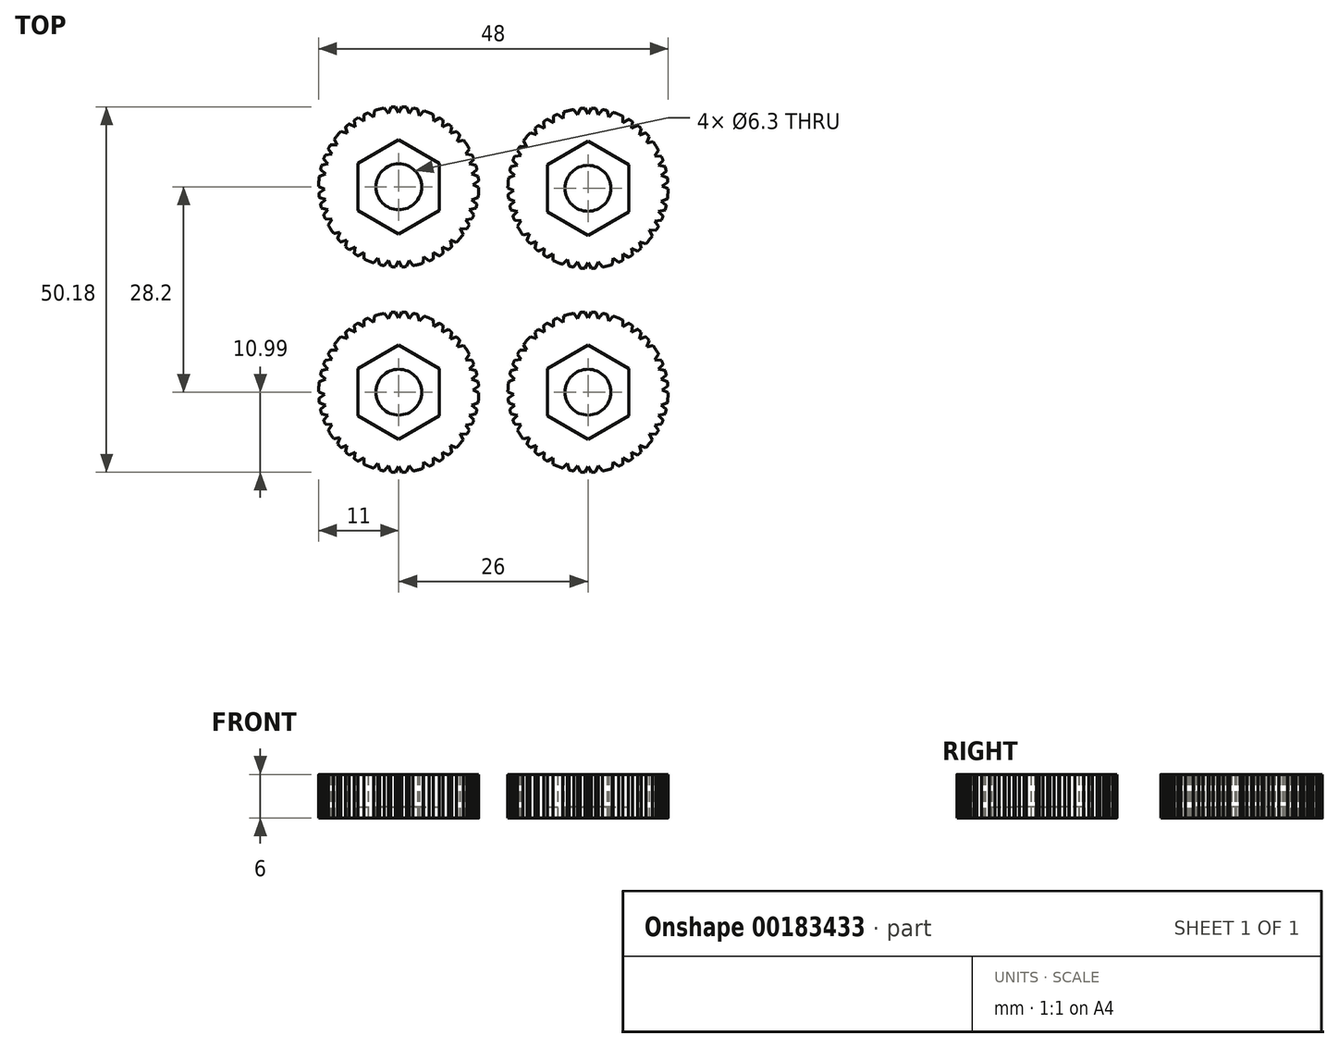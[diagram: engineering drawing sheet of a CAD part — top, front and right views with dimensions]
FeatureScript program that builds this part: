
annotation { "Feature Type Name" : "Feature", "Feature Type Description" : "" }
export const myFeature = defineFeature(function(context is Context, id is Id, definition is map)
    precondition{}
    {
        {
            var Q0;
            Q0=qCreatedBy(makeId("Top.planeOp"),FACE);
            var sketch = newSketch(context, id + "F0", { "sketchPlane" : qUnion([Q0])});
            skCircle(sketch, "E0", {"center": v(0, 0) * mm, "radius": 11 * mm});
            skCircle(sketch, "E1.cCircle", {"center": v(0, 11) * mm, "radius": 0.4 * mm, "construction": true});
            skLineSegment(sketch, "E1.0", {"start": v(-0.7, 11.4) * mm, "end": v(0.7, 11.4) * mm});
            skLineSegment(sketch, "E1.1", {"start": v(0.7, 11.4) * mm, "end": v(0, 10.2) * mm});
            skLineSegment(sketch, "E1.2", {"start": v(0, 10.2) * mm, "end": v(-0.7, 11.4) * mm});
            skPoint(sketch, "E1.0.midPoint", {"position": v(0, 11.4) * mm});
            skLineSegment(sketch, "E2.1.0", {"start": v(-6, 8.25) * mm, "end": v(-7.26, 8.82) * mm});
            skCircle(sketch, "E2.1.1", {"center": v(-6.47, 8.9) * mm, "radius": 0.4 * mm, "construction": true});
            skPoint(sketch, "E2.1.2", {"position": v(-6.7, 9.22) * mm});
            skLineSegment(sketch, "E2.1.3", {"start": v(-7.26, 8.82) * mm, "end": v(-6.14, 9.63) * mm});
            skLineSegment(sketch, "E2.1.4", {"start": v(-6.14, 9.63) * mm, "end": v(-6, 8.25) * mm});
            skLineSegment(sketch, "E2.2.0", {"start": v(-9.7, 3.15) * mm, "end": v(-11.06, 2.86) * mm});
            skCircle(sketch, "E2.2.1", {"center": v(-10.46, 3.4) * mm, "radius": 0.4 * mm, "construction": true});
            skPoint(sketch, "E2.2.2", {"position": v(-10.84, 3.52) * mm});
            skLineSegment(sketch, "E2.2.3", {"start": v(-11.06, 2.86) * mm, "end": v(-10.63, 4.18) * mm});
            skLineSegment(sketch, "E2.2.4", {"start": v(-10.63, 4.18) * mm, "end": v(-9.7, 3.15) * mm});
            skLineSegment(sketch, "E2.3.0", {"start": v(-9.7, -3.15) * mm, "end": v(-10.63, -4.18) * mm});
            skCircle(sketch, "E2.3.1", {"center": v(-10.46, -3.4) * mm, "radius": 0.4 * mm, "construction": true});
            skPoint(sketch, "E2.3.2", {"position": v(-10.84, -3.52) * mm});
            skLineSegment(sketch, "E2.3.3", {"start": v(-10.63, -4.18) * mm, "end": v(-11.06, -2.86) * mm});
            skLineSegment(sketch, "E2.3.4", {"start": v(-11.06, -2.86) * mm, "end": v(-9.7, -3.15) * mm});
            skLineSegment(sketch, "E2.4.0", {"start": v(-6, -8.25) * mm, "end": v(-6.14, -9.63) * mm});
            skCircle(sketch, "E2.4.1", {"center": v(-6.47, -8.9) * mm, "radius": 0.4 * mm, "construction": true});
            skPoint(sketch, "E2.4.2", {"position": v(-6.7, -9.22) * mm});
            skLineSegment(sketch, "E2.4.3", {"start": v(-6.14, -9.63) * mm, "end": v(-7.26, -8.82) * mm});
            skLineSegment(sketch, "E2.4.4", {"start": v(-7.26, -8.82) * mm, "end": v(-6, -8.25) * mm});
            skLineSegment(sketch, "E2.5.0", {"start": v(0, -10.2) * mm, "end": v(0.7, -11.4) * mm});
            skCircle(sketch, "E2.5.1", {"center": v(0, -11) * mm, "radius": 0.4 * mm, "construction": true});
            skPoint(sketch, "E2.5.2", {"position": v(0, -11.4) * mm});
            skLineSegment(sketch, "E2.5.3", {"start": v(0.7, -11.4) * mm, "end": v(-0.7, -11.4) * mm});
            skLineSegment(sketch, "E2.5.4", {"start": v(-0.7, -11.4) * mm, "end": v(0, -10.2) * mm});
            skLineSegment(sketch, "E2.6.0", {"start": v(6, -8.25) * mm, "end": v(7.26, -8.82) * mm});
            skCircle(sketch, "E2.6.1", {"center": v(6.47, -8.9) * mm, "radius": 0.4 * mm, "construction": true});
            skPoint(sketch, "E2.6.2", {"position": v(6.7, -9.22) * mm});
            skLineSegment(sketch, "E2.6.3", {"start": v(7.26, -8.82) * mm, "end": v(6.14, -9.63) * mm});
            skLineSegment(sketch, "E2.6.4", {"start": v(6.14, -9.63) * mm, "end": v(6, -8.25) * mm});
            skLineSegment(sketch, "E2.7.0", {"start": v(9.7, -3.15) * mm, "end": v(11.06, -2.86) * mm});
            skCircle(sketch, "E2.7.1", {"center": v(10.46, -3.4) * mm, "radius": 0.4 * mm, "construction": true});
            skPoint(sketch, "E2.7.2", {"position": v(10.84, -3.52) * mm});
            skLineSegment(sketch, "E2.7.3", {"start": v(11.06, -2.86) * mm, "end": v(10.63, -4.18) * mm});
            skLineSegment(sketch, "E2.7.4", {"start": v(10.63, -4.18) * mm, "end": v(9.7, -3.15) * mm});
            skLineSegment(sketch, "E2.8.0", {"start": v(9.7, 3.15) * mm, "end": v(10.63, 4.18) * mm});
            skCircle(sketch, "E2.8.1", {"center": v(10.46, 3.4) * mm, "radius": 0.4 * mm, "construction": true});
            skPoint(sketch, "E2.8.2", {"position": v(10.84, 3.52) * mm});
            skLineSegment(sketch, "E2.8.3", {"start": v(10.63, 4.18) * mm, "end": v(11.06, 2.86) * mm});
            skLineSegment(sketch, "E2.8.4", {"start": v(11.06, 2.86) * mm, "end": v(9.7, 3.15) * mm});
            skLineSegment(sketch, "E2.9.0", {"start": v(6, 8.25) * mm, "end": v(6.14, 9.63) * mm});
            skCircle(sketch, "E2.9.1", {"center": v(6.47, 8.9) * mm, "radius": 0.4 * mm, "construction": true});
            skPoint(sketch, "E2.9.2", {"position": v(6.7, 9.22) * mm});
            skLineSegment(sketch, "E2.9.3", {"start": v(6.14, 9.63) * mm, "end": v(7.26, 8.82) * mm});
            skLineSegment(sketch, "E2.9.4", {"start": v(7.26, 8.82) * mm, "end": v(6, 8.25) * mm});
            skCircle(sketch, "E3.cCircle", {"center": v(-9.89, 4.82) * mm, "radius": 0.4 * mm, "construction": true});
            skLineSegment(sketch, "E3.0", {"start": v(-9.16, 4.49) * mm, "end": v(-10.54, 4.35) * mm});
            skLineSegment(sketch, "E3.1", {"start": v(-10.54, 4.35) * mm, "end": v(-9.96, 5.61) * mm});
            skLineSegment(sketch, "E3.2", {"start": v(-9.96, 5.61) * mm, "end": v(-9.16, 4.49) * mm});
            skPoint(sketch, "E3.0.midPoint", {"position": v(-9.85, 4.42) * mm});
            skLineSegment(sketch, "E4.1.0", {"start": v(-11.36, -1.31) * mm, "end": v(-10.05, -1.75) * mm});
            skLineSegment(sketch, "E4.1.1", {"start": v(-11.09, -2.67) * mm, "end": v(-11.36, -1.31) * mm});
            skLineSegment(sketch, "E4.1.2", {"start": v(-10.05, -1.75) * mm, "end": v(-11.09, -2.67) * mm});
            skCircle(sketch, "E4.1.3", {"center": v(-10.83, -1.91) * mm, "radius": 0.4 * mm, "construction": true});
            skLineSegment(sketch, "E4.2.0", {"start": v(-8.42, -7.74) * mm, "end": v(-7.1, -7.33) * mm});
            skLineSegment(sketch, "E4.2.1", {"start": v(-7.4, -8.68) * mm, "end": v(-8.42, -7.74) * mm});
            skLineSegment(sketch, "E4.2.2", {"start": v(-7.1, -7.33) * mm, "end": v(-7.4, -8.68) * mm});
            skCircle(sketch, "E4.2.3", {"center": v(-7.64, -7.92) * mm, "radius": 0.4 * mm, "construction": true});
            skLineSegment(sketch, "E4.3.0", {"start": v(-2.26, -11.21) * mm, "end": v(-1.44, -10.1) * mm});
            skLineSegment(sketch, "E4.3.1", {"start": v(-0.88, -11.37) * mm, "end": v(-2.26, -11.21) * mm});
            skLineSegment(sketch, "E4.3.2", {"start": v(-1.44, -10.1) * mm, "end": v(-0.88, -11.37) * mm});
            skCircle(sketch, "E4.3.3", {"center": v(-1.53, -10.9) * mm, "radius": 0.4 * mm, "construction": true});
            skLineSegment(sketch, "E4.4.0", {"start": v(4.76, -10.4) * mm, "end": v(4.77, -9.01) * mm});
            skLineSegment(sketch, "E4.4.1", {"start": v(5.97, -9.72) * mm, "end": v(4.76, -10.4) * mm});
            skLineSegment(sketch, "E4.4.2", {"start": v(4.77, -9.01) * mm, "end": v(5.97, -9.72) * mm});
            skCircle(sketch, "E4.4.3", {"center": v(5.17, -9.71) * mm, "radius": 0.4 * mm, "construction": true});
            skLineSegment(sketch, "E4.5.0", {"start": v(9.96, -5.61) * mm, "end": v(9.16, -4.49) * mm});
            skLineSegment(sketch, "E4.5.1", {"start": v(10.54, -4.35) * mm, "end": v(9.96, -5.61) * mm});
            skLineSegment(sketch, "E4.5.2", {"start": v(9.16, -4.49) * mm, "end": v(10.54, -4.35) * mm});
            skCircle(sketch, "E4.5.3", {"center": v(9.89, -4.82) * mm, "radius": 0.4 * mm, "construction": true});
            skLineSegment(sketch, "E4.6.0", {"start": v(11.36, 1.31) * mm, "end": v(10.05, 1.75) * mm});
            skLineSegment(sketch, "E4.6.1", {"start": v(11.09, 2.67) * mm, "end": v(11.36, 1.31) * mm});
            skLineSegment(sketch, "E4.6.2", {"start": v(10.05, 1.75) * mm, "end": v(11.09, 2.67) * mm});
            skCircle(sketch, "E4.6.3", {"center": v(10.83, 1.91) * mm, "radius": 0.4 * mm, "construction": true});
            skLineSegment(sketch, "E4.7.0", {"start": v(8.42, 7.74) * mm, "end": v(7.1, 7.33) * mm});
            skLineSegment(sketch, "E4.7.1", {"start": v(7.4, 8.68) * mm, "end": v(8.42, 7.74) * mm});
            skLineSegment(sketch, "E4.7.2", {"start": v(7.1, 7.33) * mm, "end": v(7.4, 8.68) * mm});
            skCircle(sketch, "E4.7.3", {"center": v(7.64, 7.92) * mm, "radius": 0.4 * mm, "construction": true});
            skLineSegment(sketch, "E4.8.0", {"start": v(2.26, 11.21) * mm, "end": v(1.44, 10.1) * mm});
            skLineSegment(sketch, "E4.8.1", {"start": v(0.88, 11.37) * mm, "end": v(2.26, 11.21) * mm});
            skLineSegment(sketch, "E4.8.2", {"start": v(1.44, 10.1) * mm, "end": v(0.88, 11.37) * mm});
            skCircle(sketch, "E4.8.3", {"center": v(1.53, 10.9) * mm, "radius": 0.4 * mm, "construction": true});
            skLineSegment(sketch, "E4.9.0", {"start": v(-4.76, 10.4) * mm, "end": v(-4.77, 9.01) * mm});
            skLineSegment(sketch, "E4.9.1", {"start": v(-5.97, 9.72) * mm, "end": v(-4.76, 10.4) * mm});
            skLineSegment(sketch, "E4.9.2", {"start": v(-4.77, 9.01) * mm, "end": v(-5.97, 9.72) * mm});
            skCircle(sketch, "E4.9.3", {"center": v(-5.17, 9.71) * mm, "radius": 0.4 * mm, "construction": true});
            skCircle(sketch, "E5.cCircle", {"center": v(-9.11, 6.16) * mm, "radius": 0.4 * mm, "construction": true});
            skLineSegment(sketch, "E5.0", {"start": v(-9.09, 6.96) * mm, "end": v(-8.43, 5.75) * mm});
            skLineSegment(sketch, "E5.1", {"start": v(-8.43, 5.75) * mm, "end": v(-9.81, 5.78) * mm});
            skLineSegment(sketch, "E5.2", {"start": v(-9.81, 5.78) * mm, "end": v(-9.09, 6.96) * mm});
            skPoint(sketch, "E5.0.midPoint", {"position": v(-8.76, 6.35) * mm});
            skLineSegment(sketch, "E6.1.0", {"start": v(-11.34, -1.09) * mm, "end": v(-11.45, 0.3) * mm});
            skLineSegment(sketch, "E6.1.1", {"start": v(-10.2, -0.3) * mm, "end": v(-11.34, -1.09) * mm});
            skPoint(sketch, "E6.1.2", {"position": v(-10.82, 0) * mm});
            skCircle(sketch, "E6.1.3", {"center": v(-11, -0.37) * mm, "radius": 0.4 * mm, "construction": true});
            skLineSegment(sketch, "E6.1.4", {"start": v(-11.45, 0.3) * mm, "end": v(-10.2, -0.3) * mm});
            skLineSegment(sketch, "E6.2.0", {"start": v(-8.53, -7.55) * mm, "end": v(-9.43, -6.5) * mm});
            skLineSegment(sketch, "E6.2.1", {"start": v(-8.07, -6.24) * mm, "end": v(-8.53, -7.55) * mm});
            skPoint(sketch, "E6.2.2", {"position": v(-8.75, -6.37) * mm});
            skCircle(sketch, "E6.2.3", {"center": v(-8.68, -6.76) * mm, "radius": 0.4 * mm, "construction": true});
            skLineSegment(sketch, "E6.2.4", {"start": v(-9.43, -6.5) * mm, "end": v(-8.07, -6.24) * mm});
            skLineSegment(sketch, "E6.3.0", {"start": v(-2.47, -11.12) * mm, "end": v(-3.82, -10.8) * mm});
            skLineSegment(sketch, "E6.3.1", {"start": v(-2.86, -9.8) * mm, "end": v(-2.47, -11.12) * mm});
            skPoint(sketch, "E6.3.2", {"position": v(-3.34, -10.3) * mm});
            skCircle(sketch, "E6.3.3", {"center": v(-3.05, -10.57) * mm, "radius": 0.4 * mm, "construction": true});
            skLineSegment(sketch, "E6.3.4", {"start": v(-3.82, -10.8) * mm, "end": v(-2.86, -9.8) * mm});
            skLineSegment(sketch, "E6.4.0", {"start": v(4.54, -10.45) * mm, "end": v(3.26, -10.98) * mm});
            skLineSegment(sketch, "E6.4.1", {"start": v(3.44, -9.6) * mm, "end": v(4.54, -10.45) * mm});
            skPoint(sketch, "E6.4.2", {"position": v(3.35, -10.29) * mm});
            skCircle(sketch, "E6.4.3", {"center": v(3.75, -10.34) * mm, "radius": 0.4 * mm, "construction": true});
            skLineSegment(sketch, "E6.4.4", {"start": v(3.26, -10.98) * mm, "end": v(3.44, -9.6) * mm});
            skLineSegment(sketch, "E6.5.0", {"start": v(9.81, -5.78) * mm, "end": v(9.09, -6.96) * mm});
            skLineSegment(sketch, "E6.5.1", {"start": v(8.43, -5.75) * mm, "end": v(9.81, -5.78) * mm});
            skPoint(sketch, "E6.5.2", {"position": v(8.76, -6.35) * mm});
            skCircle(sketch, "E6.5.3", {"center": v(9.11, -6.16) * mm, "radius": 0.4 * mm, "construction": true});
            skLineSegment(sketch, "E6.5.4", {"start": v(9.09, -6.96) * mm, "end": v(8.43, -5.75) * mm});
            skLineSegment(sketch, "E6.6.0", {"start": v(11.34, 1.09) * mm, "end": v(11.45, -0.3) * mm});
            skLineSegment(sketch, "E6.6.1", {"start": v(10.2, 0.3) * mm, "end": v(11.34, 1.09) * mm});
            skPoint(sketch, "E6.6.2", {"position": v(10.82, 0) * mm});
            skCircle(sketch, "E6.6.3", {"center": v(11, 0.37) * mm, "radius": 0.4 * mm, "construction": true});
            skLineSegment(sketch, "E6.6.4", {"start": v(11.45, -0.3) * mm, "end": v(10.2, 0.3) * mm});
            skLineSegment(sketch, "E6.7.0", {"start": v(8.53, 7.55) * mm, "end": v(9.43, 6.5) * mm});
            skLineSegment(sketch, "E6.7.1", {"start": v(8.07, 6.24) * mm, "end": v(8.53, 7.55) * mm});
            skPoint(sketch, "E6.7.2", {"position": v(8.75, 6.37) * mm});
            skCircle(sketch, "E6.7.3", {"center": v(8.68, 6.76) * mm, "radius": 0.4 * mm, "construction": true});
            skLineSegment(sketch, "E6.7.4", {"start": v(9.43, 6.5) * mm, "end": v(8.07, 6.24) * mm});
            skLineSegment(sketch, "E6.8.0", {"start": v(2.47, 11.12) * mm, "end": v(3.82, 10.8) * mm});
            skLineSegment(sketch, "E6.8.1", {"start": v(2.86, 9.8) * mm, "end": v(2.47, 11.12) * mm});
            skPoint(sketch, "E6.8.2", {"position": v(3.34, 10.3) * mm});
            skCircle(sketch, "E6.8.3", {"center": v(3.05, 10.57) * mm, "radius": 0.4 * mm, "construction": true});
            skLineSegment(sketch, "E6.8.4", {"start": v(3.82, 10.8) * mm, "end": v(2.86, 9.8) * mm});
            skLineSegment(sketch, "E6.9.0", {"start": v(-4.54, 10.45) * mm, "end": v(-3.26, 10.98) * mm});
            skLineSegment(sketch, "E6.9.1", {"start": v(-3.44, 9.6) * mm, "end": v(-4.54, 10.45) * mm});
            skPoint(sketch, "E6.9.2", {"position": v(-3.35, 10.29) * mm});
            skCircle(sketch, "E6.9.3", {"center": v(-3.75, 10.34) * mm, "radius": 0.4 * mm, "construction": true});
            skLineSegment(sketch, "E6.9.4", {"start": v(-3.26, 10.98) * mm, "end": v(-3.44, 9.6) * mm});
            skCircle(sketch, "E7.cCircle", {"center": v(-5.18, -9.7) * mm, "radius": 0.4 * mm, "construction": true});
            skLineSegment(sketch, "E7.0", {"start": v(-5.98, -9.71) * mm, "end": v(-4.79, -9) * mm});
            skLineSegment(sketch, "E7.1", {"start": v(-4.79, -9) * mm, "end": v(-4.77, -10.4) * mm});
            skLineSegment(sketch, "E7.2", {"start": v(-4.77, -10.4) * mm, "end": v(-5.98, -9.71) * mm});
            skPoint(sketch, "E7.0.midPoint", {"position": v(-5.38, -9.36) * mm});
            skLineSegment(sketch, "E8.1.0", {"start": v(1.42, -10.1) * mm, "end": v(2.25, -11.21) * mm});
            skLineSegment(sketch, "E8.1.1", {"start": v(2.25, -11.21) * mm, "end": v(0.87, -11.37) * mm});
            skLineSegment(sketch, "E8.1.2", {"start": v(0.87, -11.37) * mm, "end": v(1.42, -10.1) * mm});
            skCircle(sketch, "E8.1.3", {"center": v(1.51, -10.9) * mm, "radius": 0.4 * mm, "construction": true});
            skLineSegment(sketch, "E8.2.0", {"start": v(7.09, -7.34) * mm, "end": v(8.4, -7.75) * mm});
            skLineSegment(sketch, "E8.2.1", {"start": v(8.4, -7.75) * mm, "end": v(7.4, -8.69) * mm});
            skLineSegment(sketch, "E8.2.2", {"start": v(7.4, -8.69) * mm, "end": v(7.09, -7.34) * mm});
            skCircle(sketch, "E8.2.3", {"center": v(7.63, -7.92) * mm, "radius": 0.4 * mm, "construction": true});
            skLineSegment(sketch, "E8.3.0", {"start": v(10.05, -1.77) * mm, "end": v(11.36, -1.33) * mm});
            skLineSegment(sketch, "E8.3.1", {"start": v(11.36, -1.33) * mm, "end": v(11.09, -2.68) * mm});
            skLineSegment(sketch, "E8.3.2", {"start": v(11.09, -2.68) * mm, "end": v(10.05, -1.77) * mm});
            skCircle(sketch, "E8.3.3", {"center": v(10.83, -1.93) * mm, "radius": 0.4 * mm, "construction": true});
            skLineSegment(sketch, "E8.4.0", {"start": v(9.17, 4.47) * mm, "end": v(9.97, 5.6) * mm});
            skLineSegment(sketch, "E8.4.1", {"start": v(9.97, 5.6) * mm, "end": v(10.55, 4.34) * mm});
            skLineSegment(sketch, "E8.4.2", {"start": v(10.55, 4.34) * mm, "end": v(9.17, 4.47) * mm});
            skCircle(sketch, "E8.4.3", {"center": v(9.9, 4.8) * mm, "radius": 0.4 * mm, "construction": true});
            skLineSegment(sketch, "E8.5.0", {"start": v(4.79, 9) * mm, "end": v(4.77, 10.4) * mm});
            skLineSegment(sketch, "E8.5.1", {"start": v(4.77, 10.4) * mm, "end": v(5.98, 9.71) * mm});
            skLineSegment(sketch, "E8.5.2", {"start": v(5.98, 9.71) * mm, "end": v(4.79, 9) * mm});
            skCircle(sketch, "E8.5.3", {"center": v(5.18, 9.7) * mm, "radius": 0.4 * mm, "construction": true});
            skLineSegment(sketch, "E8.6.0", {"start": v(-1.42, 10.1) * mm, "end": v(-2.25, 11.21) * mm});
            skLineSegment(sketch, "E8.6.1", {"start": v(-2.25, 11.21) * mm, "end": v(-0.87, 11.37) * mm});
            skLineSegment(sketch, "E8.6.2", {"start": v(-0.87, 11.37) * mm, "end": v(-1.42, 10.1) * mm});
            skCircle(sketch, "E8.6.3", {"center": v(-1.51, 10.9) * mm, "radius": 0.4 * mm, "construction": true});
            skLineSegment(sketch, "E8.7.0", {"start": v(-7.09, 7.34) * mm, "end": v(-8.4, 7.75) * mm});
            skLineSegment(sketch, "E8.7.1", {"start": v(-8.4, 7.75) * mm, "end": v(-7.4, 8.69) * mm});
            skLineSegment(sketch, "E8.7.2", {"start": v(-7.4, 8.69) * mm, "end": v(-7.09, 7.34) * mm});
            skCircle(sketch, "E8.7.3", {"center": v(-7.63, 7.92) * mm, "radius": 0.4 * mm, "construction": true});
            skLineSegment(sketch, "E8.8.0", {"start": v(-10.05, 1.77) * mm, "end": v(-11.36, 1.33) * mm});
            skLineSegment(sketch, "E8.8.1", {"start": v(-11.36, 1.33) * mm, "end": v(-11.09, 2.68) * mm});
            skLineSegment(sketch, "E8.8.2", {"start": v(-11.09, 2.68) * mm, "end": v(-10.05, 1.77) * mm});
            skCircle(sketch, "E8.8.3", {"center": v(-10.83, 1.93) * mm, "radius": 0.4 * mm, "construction": true});
            skLineSegment(sketch, "E8.9.0", {"start": v(-9.17, -4.47) * mm, "end": v(-9.97, -5.6) * mm});
            skLineSegment(sketch, "E8.9.1", {"start": v(-9.97, -5.6) * mm, "end": v(-10.55, -4.34) * mm});
            skLineSegment(sketch, "E8.9.2", {"start": v(-10.55, -4.34) * mm, "end": v(-9.17, -4.47) * mm});
            skCircle(sketch, "E8.9.3", {"center": v(-9.9, -4.8) * mm, "radius": 0.4 * mm, "construction": true});
            skSolve(sketch);
        }
        {
            var Q0;
            Q0=makeQuery(id+"F0.imprint","IMPRINT",FACE,{"disambiguationData":[TD([[makeQuery(id+"F0.imprint","IMPRINT",EDGE,{"derivedFrom":sQuery(id+"F0.wireOp",EDGE,"E0")}),1.0]])]});
            var Q1;
            Q1=sQuery(id+"F0.wireOp",EDGE,"E0");
            extrude(context, id + "F1", {"entities" : qUnion([Q0]), "surfaceEntities" : qUnion([Q1]), "depth" : 6 * mm});
        }
        {
            var Q0;
            Q0=makeQuery(id+"F1.opExtrude","CAP_FACE",FACE,{"disambiguationData":[OSD([sQuery(id+"F0.wireOp",EDGE,"E0")])],"isStart":false});
            var sketch = newSketch(context, id + "F2", { "sketchPlane" : qUnion([Q0])});
            skCircle(sketch, "E9.cCircle", {"center": v(0, 0) * mm, "radius": 5.6 * mm, "construction": true});
            skLineSegment(sketch, "E9.0", {"start": v(5.6, 3.23) * mm, "end": v(5.6, -3.23) * mm});
            skLineSegment(sketch, "E9.1", {"start": v(5.6, -3.23) * mm, "end": v(0, -6.47) * mm});
            skLineSegment(sketch, "E9.2", {"start": v(0, -6.47) * mm, "end": v(-5.6, -3.23) * mm});
            skLineSegment(sketch, "E9.3", {"start": v(-5.6, -3.23) * mm, "end": v(-5.6, 3.23) * mm});
            skLineSegment(sketch, "E9.4", {"start": v(-5.6, 3.23) * mm, "end": v(0, 6.47) * mm});
            skLineSegment(sketch, "E9.5", {"start": v(0, 6.47) * mm, "end": v(5.6, 3.23) * mm});
            skPoint(sketch, "E9.0.midPoint", {"position": v(5.6, 0) * mm});
            skSolve(sketch);
        }
        {
            var Q0;
            Q0=makeQuery(id+"F2.imprint","IMPRINT",FACE,{"disambiguationData":[TD([[makeQuery(id+"F2.imprint","IMPRINT",EDGE,{"derivedFrom":sQuery(id+"F2.wireOp",EDGE,"E9.0")}),-1.0]])]});
            extrude(context, id + "F3", {"entities" : qUnion([Q0]), "operationType" : NewBodyOperationType.REMOVE, "oppositeDirection" : true, "depth" : 4.5 * mm});
        }
        {
            var Q0;
            Q0=makeQuery(id+"F1.opExtrude","CAP_FACE",FACE,{"disambiguationData":[OSD([sQuery(id+"F0.wireOp",EDGE,"E0"),sQuery(id+"F0.wireOp",EDGE,"E1.1"),sQuery(id+"F0.wireOp",EDGE,"E1.2"),sQuery(id+"F0.wireOp",EDGE,"E2.1.0"),sQuery(id+"F0.wireOp",EDGE,"E2.1.4"),sQuery(id+"F0.wireOp",EDGE,"E2.2.0"),sQuery(id+"F0.wireOp",EDGE,"E2.2.4"),sQuery(id+"F0.wireOp",EDGE,"E2.3.0"),sQuery(id+"F0.wireOp",EDGE,"E2.3.4"),sQuery(id+"F0.wireOp",EDGE,"E2.4.0"),sQuery(id+"F0.wireOp",EDGE,"E2.4.4"),sQuery(id+"F0.wireOp",EDGE,"E2.5.0"),sQuery(id+"F0.wireOp",EDGE,"E2.5.4"),sQuery(id+"F0.wireOp",EDGE,"E2.6.0"),sQuery(id+"F0.wireOp",EDGE,"E2.6.4"),sQuery(id+"F0.wireOp",EDGE,"E2.7.0"),sQuery(id+"F0.wireOp",EDGE,"E2.7.4"),sQuery(id+"F0.wireOp",EDGE,"E2.8.0"),sQuery(id+"F0.wireOp",EDGE,"E2.8.4"),sQuery(id+"F0.wireOp",EDGE,"E2.9.0"),sQuery(id+"F0.wireOp",EDGE,"E2.9.4"),sQuery(id+"F0.wireOp",EDGE,"E3.0"),sQuery(id+"F0.wireOp",EDGE,"E3.2"),sQuery(id+"F0.wireOp",EDGE,"E4.1.0"),sQuery(id+"F0.wireOp",EDGE,"E4.1.2"),sQuery(id+"F0.wireOp",EDGE,"E4.2.0"),sQuery(id+"F0.wireOp",EDGE,"E4.2.2"),sQuery(id+"F0.wireOp",EDGE,"E4.3.0"),sQuery(id+"F0.wireOp",EDGE,"E4.3.2"),sQuery(id+"F0.wireOp",EDGE,"E4.4.0"),sQuery(id+"F0.wireOp",EDGE,"E4.4.2"),sQuery(id+"F0.wireOp",EDGE,"E4.5.0"),sQuery(id+"F0.wireOp",EDGE,"E4.5.2"),sQuery(id+"F0.wireOp",EDGE,"E4.6.0"),sQuery(id+"F0.wireOp",EDGE,"E4.6.2"),sQuery(id+"F0.wireOp",EDGE,"E4.7.0"),sQuery(id+"F0.wireOp",EDGE,"E4.7.2"),sQuery(id+"F0.wireOp",EDGE,"E4.8.0"),sQuery(id+"F0.wireOp",EDGE,"E4.8.2"),sQuery(id+"F0.wireOp",EDGE,"E4.9.0"),sQuery(id+"F0.wireOp",EDGE,"E4.9.2"),sQuery(id+"F0.wireOp",EDGE,"E5.0"),sQuery(id+"F0.wireOp",EDGE,"E5.1"),sQuery(id+"F0.wireOp",EDGE,"E6.1.1"),sQuery(id+"F0.wireOp",EDGE,"E6.1.4"),sQuery(id+"F0.wireOp",EDGE,"E6.2.1"),sQuery(id+"F0.wireOp",EDGE,"E6.2.4"),sQuery(id+"F0.wireOp",EDGE,"E6.3.1"),sQuery(id+"F0.wireOp",EDGE,"E6.3.4"),sQuery(id+"F0.wireOp",EDGE,"E6.4.1"),sQuery(id+"F0.wireOp",EDGE,"E6.4.4"),sQuery(id+"F0.wireOp",EDGE,"E6.5.1"),sQuery(id+"F0.wireOp",EDGE,"E6.5.4"),sQuery(id+"F0.wireOp",EDGE,"E6.6.1"),sQuery(id+"F0.wireOp",EDGE,"E6.6.4"),sQuery(id+"F0.wireOp",EDGE,"E6.7.1"),sQuery(id+"F0.wireOp",EDGE,"E6.7.4"),sQuery(id+"F0.wireOp",EDGE,"E6.8.1"),sQuery(id+"F0.wireOp",EDGE,"E6.8.4"),sQuery(id+"F0.wireOp",EDGE,"E6.9.1"),sQuery(id+"F0.wireOp",EDGE,"E6.9.4"),sQuery(id+"F0.wireOp",EDGE,"E7.0"),sQuery(id+"F0.wireOp",EDGE,"E7.1"),sQuery(id+"F0.wireOp",EDGE,"E8.1.0"),sQuery(id+"F0.wireOp",EDGE,"E8.1.2"),sQuery(id+"F0.wireOp",EDGE,"E8.2.0"),sQuery(id+"F0.wireOp",EDGE,"E8.2.2"),sQuery(id+"F0.wireOp",EDGE,"E8.3.0"),sQuery(id+"F0.wireOp",EDGE,"E8.3.2"),sQuery(id+"F0.wireOp",EDGE,"E8.4.0"),sQuery(id+"F0.wireOp",EDGE,"E8.4.2"),sQuery(id+"F0.wireOp",EDGE,"E8.5.0"),sQuery(id+"F0.wireOp",EDGE,"E8.5.2"),sQuery(id+"F0.wireOp",EDGE,"E8.6.0"),sQuery(id+"F0.wireOp",EDGE,"E8.6.2"),sQuery(id+"F0.wireOp",EDGE,"E8.7.0"),sQuery(id+"F0.wireOp",EDGE,"E8.7.2"),sQuery(id+"F0.wireOp",EDGE,"E8.8.0"),sQuery(id+"F0.wireOp",EDGE,"E8.8.2"),sQuery(id+"F0.wireOp",EDGE,"E8.9.0"),sQuery(id+"F0.wireOp",EDGE,"E8.9.2")])],"isStart":true});
            var sketch = newSketch(context, id + "F4", { "sketchPlane" : qUnion([Q0])});
            skCircle(sketch, "E10", {"center": v(0, 0) * mm, "radius": 3.15 * mm});
            skSolve(sketch);
        }
        {
            var Q0;
            Q0=makeQuery(id+"F4.imprint","IMPRINT",FACE,{"disambiguationData":[TD([[makeQuery(id+"F4.imprint","IMPRINT",EDGE,{"derivedFrom":sQuery(id+"F4.wireOp",EDGE,"E10")}),1.0]])]});
            extrude(context, id + "F5", {"entities" : qUnion([Q0]), "operationType" : NewBodyOperationType.REMOVE, "endBound" : BoundingType.THROUGH_ALL, "oppositeDirection" : true, "depth" : 25 * mm});
        }
        {
            var Q0;
            Q0=makeQuery(id+"F1.opExtrude","SWEPT_BODY",BODY,{"disambiguationData":[OSD([sQuery(id+"F0.wireOp",EDGE,"E0"),sQuery(id+"F0.wireOp",EDGE,"E1.1"),sQuery(id+"F0.wireOp",EDGE,"E1.2"),sQuery(id+"F0.wireOp",EDGE,"E2.1.0"),sQuery(id+"F0.wireOp",EDGE,"E2.1.4"),sQuery(id+"F0.wireOp",EDGE,"E2.2.0"),sQuery(id+"F0.wireOp",EDGE,"E2.2.4"),sQuery(id+"F0.wireOp",EDGE,"E2.3.0"),sQuery(id+"F0.wireOp",EDGE,"E2.3.4"),sQuery(id+"F0.wireOp",EDGE,"E2.4.0"),sQuery(id+"F0.wireOp",EDGE,"E2.4.4"),sQuery(id+"F0.wireOp",EDGE,"E2.5.0"),sQuery(id+"F0.wireOp",EDGE,"E2.5.4"),sQuery(id+"F0.wireOp",EDGE,"E2.6.0"),sQuery(id+"F0.wireOp",EDGE,"E2.6.4"),sQuery(id+"F0.wireOp",EDGE,"E2.7.0"),sQuery(id+"F0.wireOp",EDGE,"E2.7.4"),sQuery(id+"F0.wireOp",EDGE,"E2.8.0"),sQuery(id+"F0.wireOp",EDGE,"E2.8.4"),sQuery(id+"F0.wireOp",EDGE,"E2.9.0"),sQuery(id+"F0.wireOp",EDGE,"E2.9.4"),sQuery(id+"F0.wireOp",EDGE,"E3.0"),sQuery(id+"F0.wireOp",EDGE,"E3.2"),sQuery(id+"F0.wireOp",EDGE,"E4.1.0"),sQuery(id+"F0.wireOp",EDGE,"E4.1.2"),sQuery(id+"F0.wireOp",EDGE,"E4.2.0"),sQuery(id+"F0.wireOp",EDGE,"E4.2.2"),sQuery(id+"F0.wireOp",EDGE,"E4.3.0"),sQuery(id+"F0.wireOp",EDGE,"E4.3.2"),sQuery(id+"F0.wireOp",EDGE,"E4.4.0"),sQuery(id+"F0.wireOp",EDGE,"E4.4.2"),sQuery(id+"F0.wireOp",EDGE,"E4.5.0"),sQuery(id+"F0.wireOp",EDGE,"E4.5.2"),sQuery(id+"F0.wireOp",EDGE,"E4.6.0"),sQuery(id+"F0.wireOp",EDGE,"E4.6.2"),sQuery(id+"F0.wireOp",EDGE,"E4.7.0"),sQuery(id+"F0.wireOp",EDGE,"E4.7.2"),sQuery(id+"F0.wireOp",EDGE,"E4.8.0"),sQuery(id+"F0.wireOp",EDGE,"E4.8.2"),sQuery(id+"F0.wireOp",EDGE,"E4.9.0"),sQuery(id+"F0.wireOp",EDGE,"E4.9.2"),sQuery(id+"F0.wireOp",EDGE,"E5.0"),sQuery(id+"F0.wireOp",EDGE,"E5.1"),sQuery(id+"F0.wireOp",EDGE,"E6.1.1"),sQuery(id+"F0.wireOp",EDGE,"E6.1.4"),sQuery(id+"F0.wireOp",EDGE,"E6.2.1"),sQuery(id+"F0.wireOp",EDGE,"E6.2.4"),sQuery(id+"F0.wireOp",EDGE,"E6.3.1"),sQuery(id+"F0.wireOp",EDGE,"E6.3.4"),sQuery(id+"F0.wireOp",EDGE,"E6.4.1"),sQuery(id+"F0.wireOp",EDGE,"E6.4.4"),sQuery(id+"F0.wireOp",EDGE,"E6.5.1"),sQuery(id+"F0.wireOp",EDGE,"E6.5.4"),sQuery(id+"F0.wireOp",EDGE,"E6.6.1"),sQuery(id+"F0.wireOp",EDGE,"E6.6.4"),sQuery(id+"F0.wireOp",EDGE,"E6.7.1"),sQuery(id+"F0.wireOp",EDGE,"E6.7.4"),sQuery(id+"F0.wireOp",EDGE,"E6.8.1"),sQuery(id+"F0.wireOp",EDGE,"E6.8.4"),sQuery(id+"F0.wireOp",EDGE,"E6.9.1"),sQuery(id+"F0.wireOp",EDGE,"E6.9.4"),sQuery(id+"F0.wireOp",EDGE,"E7.0"),sQuery(id+"F0.wireOp",EDGE,"E7.1"),sQuery(id+"F0.wireOp",EDGE,"E8.1.0"),sQuery(id+"F0.wireOp",EDGE,"E8.1.2"),sQuery(id+"F0.wireOp",EDGE,"E8.2.0"),sQuery(id+"F0.wireOp",EDGE,"E8.2.2"),sQuery(id+"F0.wireOp",EDGE,"E8.3.0"),sQuery(id+"F0.wireOp",EDGE,"E8.3.2"),sQuery(id+"F0.wireOp",EDGE,"E8.4.0"),sQuery(id+"F0.wireOp",EDGE,"E8.4.2"),sQuery(id+"F0.wireOp",EDGE,"E8.5.0"),sQuery(id+"F0.wireOp",EDGE,"E8.5.2"),sQuery(id+"F0.wireOp",EDGE,"E8.6.0"),sQuery(id+"F0.wireOp",EDGE,"E8.6.2"),sQuery(id+"F0.wireOp",EDGE,"E8.7.0"),sQuery(id+"F0.wireOp",EDGE,"E8.7.2"),sQuery(id+"F0.wireOp",EDGE,"E8.8.0"),sQuery(id+"F0.wireOp",EDGE,"E8.8.2"),sQuery(id+"F0.wireOp",EDGE,"E8.9.0"),sQuery(id+"F0.wireOp",EDGE,"E8.9.2")])]});
            transform(context, id + "F6", {"entities" : qUnion([Q0]), "transformType" : TransformType.TRANSLATION_3D, "dx" : 0 * mm, "dy" : 28.2 * mm, "dz" : 0 * mm, "makeCopy" : true});
        }
        {
            var Q0;
            Q0=makeQuery(id+"F1.opExtrude","SWEPT_BODY",BODY,{"disambiguationData":[OSD([sQuery(id+"F0.wireOp",EDGE,"E0"),sQuery(id+"F0.wireOp",EDGE,"E1.1"),sQuery(id+"F0.wireOp",EDGE,"E1.2"),sQuery(id+"F0.wireOp",EDGE,"E2.1.0"),sQuery(id+"F0.wireOp",EDGE,"E2.1.4"),sQuery(id+"F0.wireOp",EDGE,"E2.2.0"),sQuery(id+"F0.wireOp",EDGE,"E2.2.4"),sQuery(id+"F0.wireOp",EDGE,"E2.3.0"),sQuery(id+"F0.wireOp",EDGE,"E2.3.4"),sQuery(id+"F0.wireOp",EDGE,"E2.4.0"),sQuery(id+"F0.wireOp",EDGE,"E2.4.4"),sQuery(id+"F0.wireOp",EDGE,"E2.5.0"),sQuery(id+"F0.wireOp",EDGE,"E2.5.4"),sQuery(id+"F0.wireOp",EDGE,"E2.6.0"),sQuery(id+"F0.wireOp",EDGE,"E2.6.4"),sQuery(id+"F0.wireOp",EDGE,"E2.7.0"),sQuery(id+"F0.wireOp",EDGE,"E2.7.4"),sQuery(id+"F0.wireOp",EDGE,"E2.8.0"),sQuery(id+"F0.wireOp",EDGE,"E2.8.4"),sQuery(id+"F0.wireOp",EDGE,"E2.9.0"),sQuery(id+"F0.wireOp",EDGE,"E2.9.4"),sQuery(id+"F0.wireOp",EDGE,"E3.0"),sQuery(id+"F0.wireOp",EDGE,"E3.2"),sQuery(id+"F0.wireOp",EDGE,"E4.1.0"),sQuery(id+"F0.wireOp",EDGE,"E4.1.2"),sQuery(id+"F0.wireOp",EDGE,"E4.2.0"),sQuery(id+"F0.wireOp",EDGE,"E4.2.2"),sQuery(id+"F0.wireOp",EDGE,"E4.3.0"),sQuery(id+"F0.wireOp",EDGE,"E4.3.2"),sQuery(id+"F0.wireOp",EDGE,"E4.4.0"),sQuery(id+"F0.wireOp",EDGE,"E4.4.2"),sQuery(id+"F0.wireOp",EDGE,"E4.5.0"),sQuery(id+"F0.wireOp",EDGE,"E4.5.2"),sQuery(id+"F0.wireOp",EDGE,"E4.6.0"),sQuery(id+"F0.wireOp",EDGE,"E4.6.2"),sQuery(id+"F0.wireOp",EDGE,"E4.7.0"),sQuery(id+"F0.wireOp",EDGE,"E4.7.2"),sQuery(id+"F0.wireOp",EDGE,"E4.8.0"),sQuery(id+"F0.wireOp",EDGE,"E4.8.2"),sQuery(id+"F0.wireOp",EDGE,"E4.9.0"),sQuery(id+"F0.wireOp",EDGE,"E4.9.2"),sQuery(id+"F0.wireOp",EDGE,"E5.0"),sQuery(id+"F0.wireOp",EDGE,"E5.1"),sQuery(id+"F0.wireOp",EDGE,"E6.1.1"),sQuery(id+"F0.wireOp",EDGE,"E6.1.4"),sQuery(id+"F0.wireOp",EDGE,"E6.2.1"),sQuery(id+"F0.wireOp",EDGE,"E6.2.4"),sQuery(id+"F0.wireOp",EDGE,"E6.3.1"),sQuery(id+"F0.wireOp",EDGE,"E6.3.4"),sQuery(id+"F0.wireOp",EDGE,"E6.4.1"),sQuery(id+"F0.wireOp",EDGE,"E6.4.4"),sQuery(id+"F0.wireOp",EDGE,"E6.5.1"),sQuery(id+"F0.wireOp",EDGE,"E6.5.4"),sQuery(id+"F0.wireOp",EDGE,"E6.6.1"),sQuery(id+"F0.wireOp",EDGE,"E6.6.4"),sQuery(id+"F0.wireOp",EDGE,"E6.7.1"),sQuery(id+"F0.wireOp",EDGE,"E6.7.4"),sQuery(id+"F0.wireOp",EDGE,"E6.8.1"),sQuery(id+"F0.wireOp",EDGE,"E6.8.4"),sQuery(id+"F0.wireOp",EDGE,"E6.9.1"),sQuery(id+"F0.wireOp",EDGE,"E6.9.4"),sQuery(id+"F0.wireOp",EDGE,"E7.0"),sQuery(id+"F0.wireOp",EDGE,"E7.1"),sQuery(id+"F0.wireOp",EDGE,"E8.1.0"),sQuery(id+"F0.wireOp",EDGE,"E8.1.2"),sQuery(id+"F0.wireOp",EDGE,"E8.2.0"),sQuery(id+"F0.wireOp",EDGE,"E8.2.2"),sQuery(id+"F0.wireOp",EDGE,"E8.3.0"),sQuery(id+"F0.wireOp",EDGE,"E8.3.2"),sQuery(id+"F0.wireOp",EDGE,"E8.4.0"),sQuery(id+"F0.wireOp",EDGE,"E8.4.2"),sQuery(id+"F0.wireOp",EDGE,"E8.5.0"),sQuery(id+"F0.wireOp",EDGE,"E8.5.2"),sQuery(id+"F0.wireOp",EDGE,"E8.6.0"),sQuery(id+"F0.wireOp",EDGE,"E8.6.2"),sQuery(id+"F0.wireOp",EDGE,"E8.7.0"),sQuery(id+"F0.wireOp",EDGE,"E8.7.2"),sQuery(id+"F0.wireOp",EDGE,"E8.8.0"),sQuery(id+"F0.wireOp",EDGE,"E8.8.2"),sQuery(id+"F0.wireOp",EDGE,"E8.9.0"),sQuery(id+"F0.wireOp",EDGE,"E8.9.2")])]});
            transform(context, id + "F7", {"entities" : qUnion([Q0]), "transformType" : TransformType.TRANSLATION_3D, "dx" : 26 * mm, "dy" : 0 * mm, "dz" : 0 * mm, "makeCopy" : true});
        }
        {
            var Q0;
            Q0=makeQuery(id+"F7.opPattern","COPY",BODY,{"derivedFrom":makeQuery(id+"F1.opExtrude","SWEPT_BODY",BODY,{"disambiguationData":[OSD([sQuery(id+"F0.wireOp",EDGE,"E0"),sQuery(id+"F0.wireOp",EDGE,"E1.1"),sQuery(id+"F0.wireOp",EDGE,"E1.2"),sQuery(id+"F0.wireOp",EDGE,"E2.1.0"),sQuery(id+"F0.wireOp",EDGE,"E2.1.4"),sQuery(id+"F0.wireOp",EDGE,"E2.2.0"),sQuery(id+"F0.wireOp",EDGE,"E2.2.4"),sQuery(id+"F0.wireOp",EDGE,"E2.3.0"),sQuery(id+"F0.wireOp",EDGE,"E2.3.4"),sQuery(id+"F0.wireOp",EDGE,"E2.4.0"),sQuery(id+"F0.wireOp",EDGE,"E2.4.4"),sQuery(id+"F0.wireOp",EDGE,"E2.5.0"),sQuery(id+"F0.wireOp",EDGE,"E2.5.4"),sQuery(id+"F0.wireOp",EDGE,"E2.6.0"),sQuery(id+"F0.wireOp",EDGE,"E2.6.4"),sQuery(id+"F0.wireOp",EDGE,"E2.7.0"),sQuery(id+"F0.wireOp",EDGE,"E2.7.4"),sQuery(id+"F0.wireOp",EDGE,"E2.8.0"),sQuery(id+"F0.wireOp",EDGE,"E2.8.4"),sQuery(id+"F0.wireOp",EDGE,"E2.9.0"),sQuery(id+"F0.wireOp",EDGE,"E2.9.4"),sQuery(id+"F0.wireOp",EDGE,"E3.0"),sQuery(id+"F0.wireOp",EDGE,"E3.2"),sQuery(id+"F0.wireOp",EDGE,"E4.1.0"),sQuery(id+"F0.wireOp",EDGE,"E4.1.2"),sQuery(id+"F0.wireOp",EDGE,"E4.2.0"),sQuery(id+"F0.wireOp",EDGE,"E4.2.2"),sQuery(id+"F0.wireOp",EDGE,"E4.3.0"),sQuery(id+"F0.wireOp",EDGE,"E4.3.2"),sQuery(id+"F0.wireOp",EDGE,"E4.4.0"),sQuery(id+"F0.wireOp",EDGE,"E4.4.2"),sQuery(id+"F0.wireOp",EDGE,"E4.5.0"),sQuery(id+"F0.wireOp",EDGE,"E4.5.2"),sQuery(id+"F0.wireOp",EDGE,"E4.6.0"),sQuery(id+"F0.wireOp",EDGE,"E4.6.2"),sQuery(id+"F0.wireOp",EDGE,"E4.7.0"),sQuery(id+"F0.wireOp",EDGE,"E4.7.2"),sQuery(id+"F0.wireOp",EDGE,"E4.8.0"),sQuery(id+"F0.wireOp",EDGE,"E4.8.2"),sQuery(id+"F0.wireOp",EDGE,"E4.9.0"),sQuery(id+"F0.wireOp",EDGE,"E4.9.2"),sQuery(id+"F0.wireOp",EDGE,"E5.0"),sQuery(id+"F0.wireOp",EDGE,"E5.1"),sQuery(id+"F0.wireOp",EDGE,"E6.1.1"),sQuery(id+"F0.wireOp",EDGE,"E6.1.4"),sQuery(id+"F0.wireOp",EDGE,"E6.2.1"),sQuery(id+"F0.wireOp",EDGE,"E6.2.4"),sQuery(id+"F0.wireOp",EDGE,"E6.3.1"),sQuery(id+"F0.wireOp",EDGE,"E6.3.4"),sQuery(id+"F0.wireOp",EDGE,"E6.4.1"),sQuery(id+"F0.wireOp",EDGE,"E6.4.4"),sQuery(id+"F0.wireOp",EDGE,"E6.5.1"),sQuery(id+"F0.wireOp",EDGE,"E6.5.4"),sQuery(id+"F0.wireOp",EDGE,"E6.6.1"),sQuery(id+"F0.wireOp",EDGE,"E6.6.4"),sQuery(id+"F0.wireOp",EDGE,"E6.7.1"),sQuery(id+"F0.wireOp",EDGE,"E6.7.4"),sQuery(id+"F0.wireOp",EDGE,"E6.8.1"),sQuery(id+"F0.wireOp",EDGE,"E6.8.4"),sQuery(id+"F0.wireOp",EDGE,"E6.9.1"),sQuery(id+"F0.wireOp",EDGE,"E6.9.4"),sQuery(id+"F0.wireOp",EDGE,"E7.0"),sQuery(id+"F0.wireOp",EDGE,"E7.1"),sQuery(id+"F0.wireOp",EDGE,"E8.1.0"),sQuery(id+"F0.wireOp",EDGE,"E8.1.2"),sQuery(id+"F0.wireOp",EDGE,"E8.2.0"),sQuery(id+"F0.wireOp",EDGE,"E8.2.2"),sQuery(id+"F0.wireOp",EDGE,"E8.3.0"),sQuery(id+"F0.wireOp",EDGE,"E8.3.2"),sQuery(id+"F0.wireOp",EDGE,"E8.4.0"),sQuery(id+"F0.wireOp",EDGE,"E8.4.2"),sQuery(id+"F0.wireOp",EDGE,"E8.5.0"),sQuery(id+"F0.wireOp",EDGE,"E8.5.2"),sQuery(id+"F0.wireOp",EDGE,"E8.6.0"),sQuery(id+"F0.wireOp",EDGE,"E8.6.2"),sQuery(id+"F0.wireOp",EDGE,"E8.7.0"),sQuery(id+"F0.wireOp",EDGE,"E8.7.2"),sQuery(id+"F0.wireOp",EDGE,"E8.8.0"),sQuery(id+"F0.wireOp",EDGE,"E8.8.2"),sQuery(id+"F0.wireOp",EDGE,"E8.9.0"),sQuery(id+"F0.wireOp",EDGE,"E8.9.2")])]}),"instanceName":"1"});
            transform(context, id + "F8", {"entities" : qUnion([Q0]), "transformType" : TransformType.TRANSLATION_3D, "dx" : 0 * mm, "dy" : 28 * mm, "dz" : 0 * mm, "makeCopy" : true});
        }
    });
